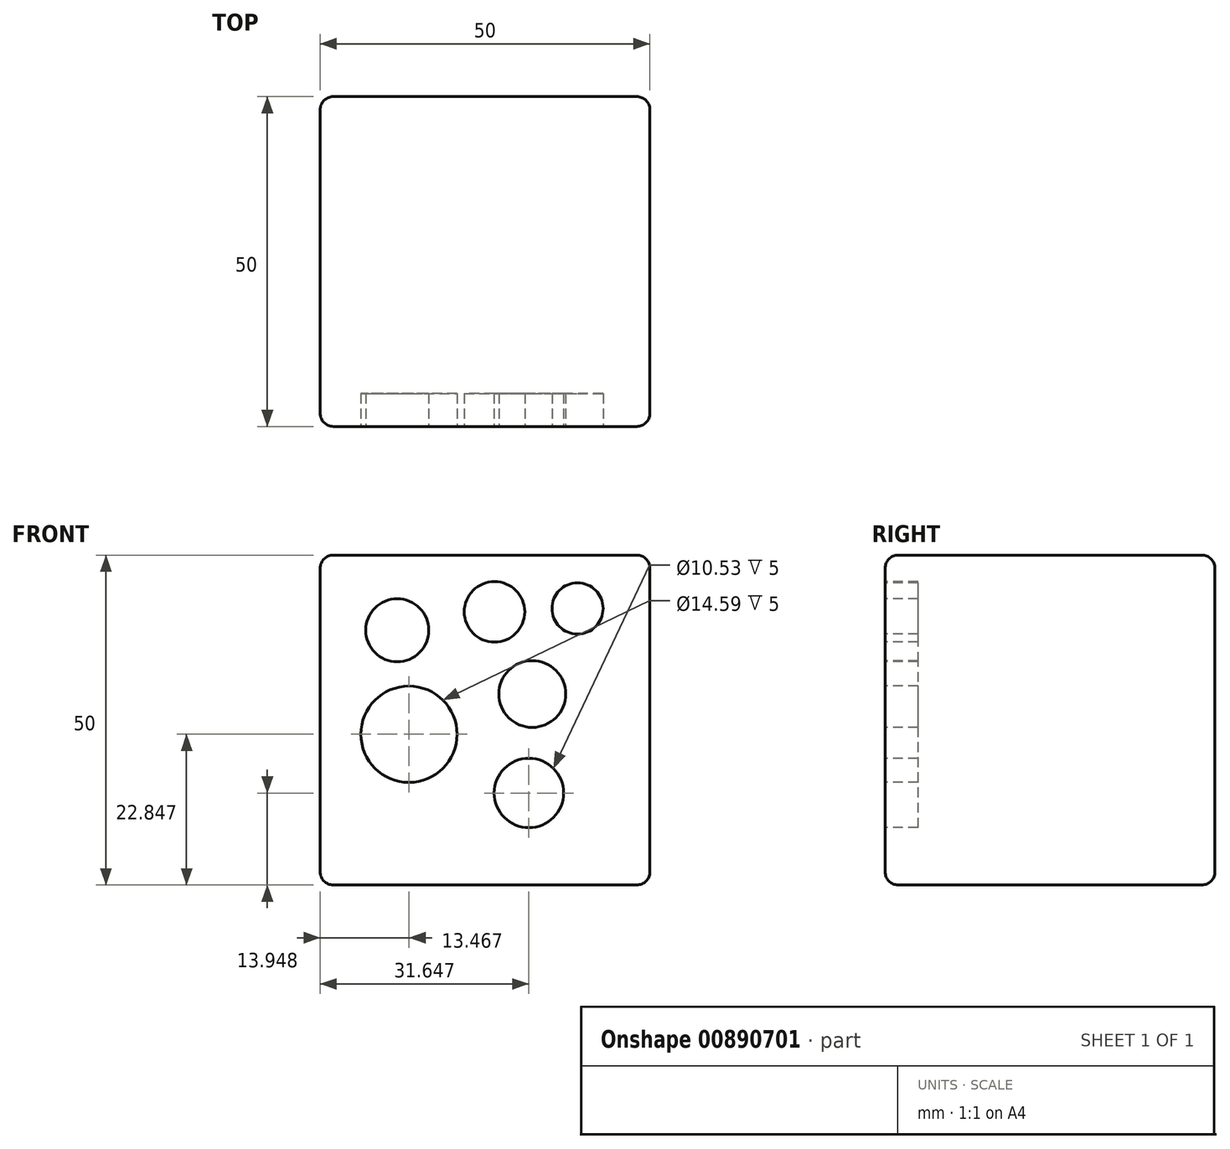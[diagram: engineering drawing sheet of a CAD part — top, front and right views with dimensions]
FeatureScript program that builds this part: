
annotation { "Feature Type Name" : "Feature", "Feature Type Description" : "" }
export const myFeature = defineFeature(function(context is Context, id is Id, definition is map)
    precondition{}
    {
        {
            var Q0;
            Q0=qCreatedBy(makeId("Front.planeOp"),FACE);
            var sketch = newSketch(context, id + "F0", { "sketchPlane" : qUnion([Q0])});
            skLineSegment(sketch, "E0.bottom", {"start": v(-21.72, 25.65) * mm, "end": v(28.28, 25.65) * mm});
            skLineSegment(sketch, "E0.top", {"start": v(-21.72, -24.35) * mm, "end": v(28.28, -24.35) * mm});
            skLineSegment(sketch, "E0.left", {"start": v(-21.72, 25.65) * mm, "end": v(-21.72, -24.35) * mm});
            skLineSegment(sketch, "E0.right", {"start": v(28.28, 25.65) * mm, "end": v(28.28, -24.35) * mm});
            skSolve(sketch);
        }
        {
            var Q0;
            Q0 = qSketchRegion(id + "F0", true);
            extrude(context, id + "F1", {"entities" : qUnion([Q0]), "depth" : 50 * mm, "offsetDistance" : 25 * mm});
        }
        {
            var Q0;
            Q0=makeQuery(id+"F1.opExtrude","SWEPT_FACE",FACE,{"disambiguationData":[OSD([sQuery(id+"F0.wireOp",EDGE,"E0.left")])]});
            var Q1;
            Q1=makeQuery(id+"F1.opExtrude","CAP_FACE",FACE,{"disambiguationData":[OSD([sQuery(id+"F0.wireOp",EDGE,"E0.bottom"),sQuery(id+"F0.wireOp",EDGE,"E0.top"),sQuery(id+"F0.wireOp",EDGE,"E0.left"),sQuery(id+"F0.wireOp",EDGE,"E0.right")])],"isStart":false});
            var Q2;
            Q2=makeQuery(id+"F1.opExtrude","SWEPT_FACE",FACE,{"disambiguationData":[OSD([sQuery(id+"F0.wireOp",EDGE,"E0.top")])]});
            var Q3;
            Q3=makeQuery(id+"F1.opExtrude","SWEPT_FACE",FACE,{"disambiguationData":[OSD([sQuery(id+"F0.wireOp",EDGE,"E0.right")])]});
            var Q4;
            Q4=makeQuery(id+"F1.opExtrude","CAP_FACE",FACE,{"disambiguationData":[OSD([sQuery(id+"F0.wireOp",EDGE,"E0.bottom"),sQuery(id+"F0.wireOp",EDGE,"E0.top"),sQuery(id+"F0.wireOp",EDGE,"E0.left"),sQuery(id+"F0.wireOp",EDGE,"E0.right")])],"isStart":true});
            fillet(context, id + "F2", {"entities" : qUnion([Q0, Q1, Q2, Q3, Q4]), "radius" : 2 * mm, "tangentPropagation" : true, "allowEdgeOverflow" : false});
        }
        {
            var Q0;
            Q0=makeQuery(id+"F1.opExtrude","CAP_FACE",FACE,{"disambiguationData":[OSD([sQuery(id+"F0.wireOp",EDGE,"E0.bottom"),sQuery(id+"F0.wireOp",EDGE,"E0.top"),sQuery(id+"F0.wireOp",EDGE,"E0.left"),sQuery(id+"F0.wireOp",EDGE,"E0.right")])],"isStart":false});
            var sketch = newSketch(context, id + "F3", { "sketchPlane" : qUnion([Q0])});
            skCircle(sketch, "E1", {"center": v(-10.03, 14.26) * mm, "radius": 4.79 * mm});
            skCircle(sketch, "E2", {"center": v(4.71, 17.06) * mm, "radius": 4.58 * mm});
            skCircle(sketch, "E3", {"center": v(10.44, 4.6) * mm, "radius": 5.06 * mm});
            skCircle(sketch, "E4", {"center": v(-8.25, -1.5) * mm, "radius": 7.3 * mm});
            skCircle(sketch, "E5", {"center": v(9.93, -10.4) * mm, "radius": 5.26 * mm});
            skCircle(sketch, "E6", {"center": v(17.3, 17.57) * mm, "radius": 3.87 * mm});
            skSolve(sketch);
        }
        {
            var Q0;
            Q0=makeQuery(id+"F3.imprint","IMPRINT",FACE,{"disambiguationData":[TD([[makeQuery(id+"F3.imprint","IMPRINT",EDGE,{"derivedFrom":sQuery(id+"F3.wireOp",EDGE,"E1")}),1.0]])]});
            var Q1;
            Q1=makeQuery(id+"F3.imprint","IMPRINT",FACE,{"disambiguationData":[TD([[makeQuery(id+"F3.imprint","IMPRINT",EDGE,{"derivedFrom":sQuery(id+"F3.wireOp",EDGE,"E4")}),1.0]])]});
            var Q2;
            Q2=makeQuery(id+"F3.imprint","IMPRINT",FACE,{"disambiguationData":[TD([[makeQuery(id+"F3.imprint","IMPRINT",EDGE,{"derivedFrom":sQuery(id+"F3.wireOp",EDGE,"E3")}),1.0]])]});
            var Q3;
            Q3=makeQuery(id+"F3.imprint","IMPRINT",FACE,{"disambiguationData":[TD([[makeQuery(id+"F3.imprint","IMPRINT",EDGE,{"derivedFrom":sQuery(id+"F3.wireOp",EDGE,"E2")}),1.0]])]});
            var Q4;
            Q4=makeQuery(id+"F3.imprint","IMPRINT",FACE,{"disambiguationData":[TD([[makeQuery(id+"F3.imprint","IMPRINT",EDGE,{"derivedFrom":sQuery(id+"F3.wireOp",EDGE,"E6")}),1.0]])]});
            var Q5;
            Q5=makeQuery(id+"F3.imprint","IMPRINT",FACE,{"disambiguationData":[TD([[makeQuery(id+"F3.imprint","IMPRINT",EDGE,{"derivedFrom":sQuery(id+"F3.wireOp",EDGE,"E5")}),1.0]])]});
            extrude(context, id + "F4", {"entities" : qUnion([Q0, Q1, Q2, Q3, Q4, Q5]), "operationType" : NewBodyOperationType.REMOVE, "oppositeDirection" : true, "depth" : 5 * mm, "offsetDistance" : 25 * mm});
        }
    });
